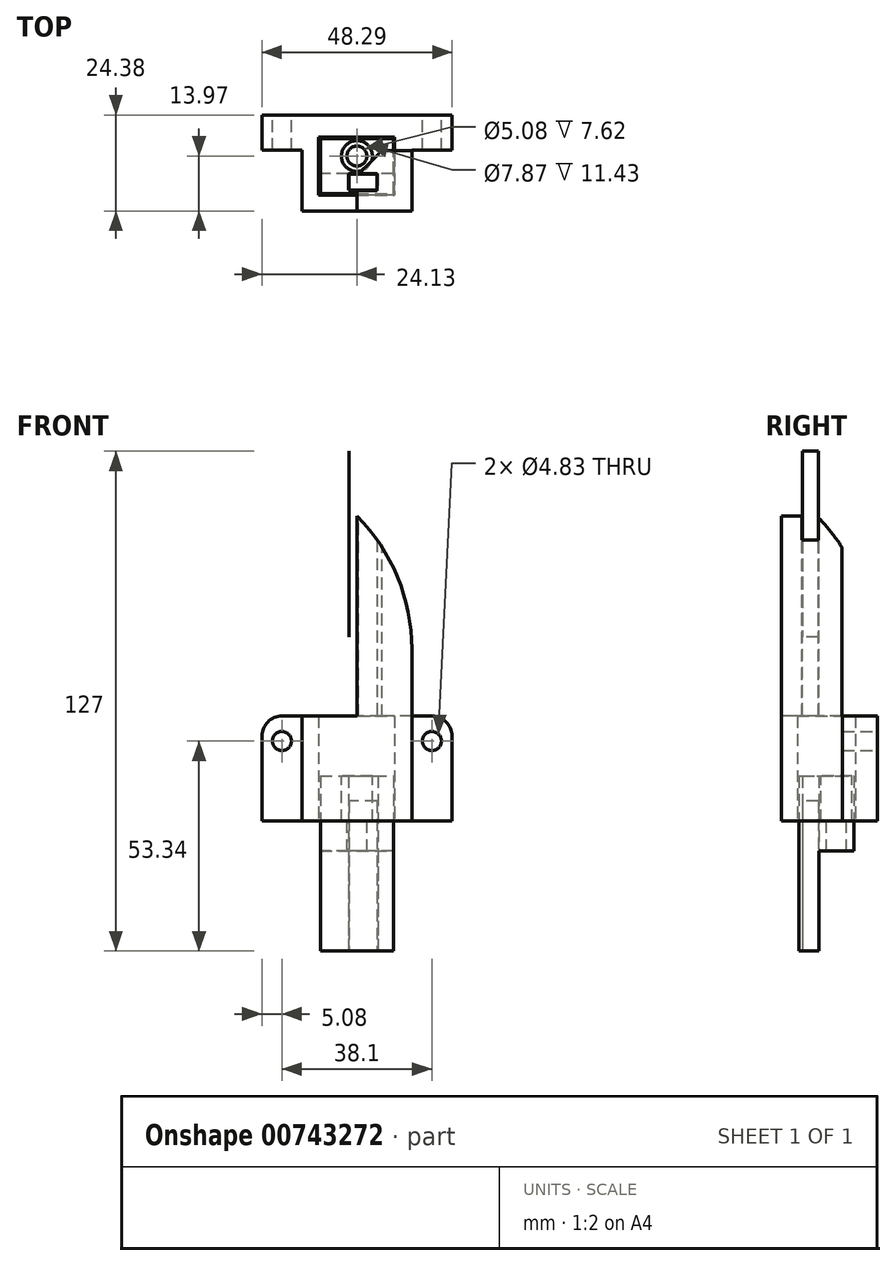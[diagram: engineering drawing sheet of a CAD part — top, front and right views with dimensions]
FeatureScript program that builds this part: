
annotation { "Feature Type Name" : "Feature", "Feature Type Description" : "" }
export const myFeature = defineFeature(function(context is Context, id is Id, definition is map)
    precondition{}
    {
        {
            var Q0;
            Q0=qCreatedBy(makeId("Top.planeOp"),FACE);
            var sketch = newSketch(context, id + "F0", { "sketchPlane" : qUnion([Q0])});
            skLineSegment(sketch, "E0.bottom", {"start": v(-9.27, -4.45) * mm, "end": v(9.27, -4.45) * mm});
            skLineSegment(sketch, "E0.top", {"start": v(-9.27, 4.45) * mm, "end": v(9.27, 4.45) * mm});
            skLineSegment(sketch, "E0.left", {"start": v(-9.27, -4.45) * mm, "end": v(-9.27, 4.45) * mm});
            skLineSegment(sketch, "E0.right", {"start": v(9.27, -4.45) * mm, "end": v(9.27, 4.45) * mm});
            skPoint(sketch, "E0.middle", {"position": v(0, 0) * mm});
            skSolve(sketch);
        }
        {
            var Q0;
            Q0 = qSketchRegion(id + "F0", true);
            extrude(context, id + "F1", {"entities" : qUnion([Q0]), "depth" : 6.35 * mm, "offsetDistance" : 25.4 * mm});
        }
        {
            var Q0;
            Q0=makeQuery(id+"F1.opExtrude","SWEPT_FACE",FACE,{"disambiguationData":[OSD([sQuery(id+"F0.wireOp",EDGE,"E0.bottom")])]});
            extrude(context, id + "F2", {"entities" : qUnion([Q0]), "operationType" : NewBodyOperationType.ADD, "depth" : 5.08 * mm, "offsetDistance" : 25.4 * mm});
        }
        {
            var Q0;
            {var subQ0=sQuery(id+"F0.wireOp",EDGE,"E0.bottom");Q0=makeQuery(id+"F2.boolean.opBoolean","MERGE",FACE,{"derivedFrom":[makeQuery(id+"F1.opExtrude","CAP_FACE",FACE,{"disambiguationData":[OSD([subQ0,sQuery(id+"F0.wireOp",EDGE,"E0.top"),sQuery(id+"F0.wireOp",EDGE,"E0.left"),sQuery(id+"F0.wireOp",EDGE,"E0.right")])],"isStart":true}),makeQuery(id+"F2.opExtrude","SWEPT_FACE",FACE,{"disambiguationData":[OSD([subQ0]),TDD([makeQuery(id+"F1.opExtrude","CAP_EDGE",EDGE,{"disambiguationData":[OSD([subQ0])],"isStart":true})])]})]});}
            var sketch = newSketch(context, id + "F3", { "sketchPlane" : qUnion([Q0])});
            skLineSegment(sketch, "E1.bottom", {"start": v(9.27, 9.53) * mm, "end": v(-9.27, 9.53) * mm});
            skLineSegment(sketch, "E1.top", {"start": v(9.27, 4.46) * mm, "end": v(-9.27, 4.46) * mm});
            skLineSegment(sketch, "E1.left", {"start": v(9.27, 9.53) * mm, "end": v(9.27, 4.46) * mm});
            skLineSegment(sketch, "E1.right", {"start": v(-9.27, 9.53) * mm, "end": v(-9.27, 4.46) * mm});
            skSolve(sketch);
        }
        {
            var Q0;
            Q0 = qSketchRegion(id + "F3", true);
            extrude(context, id + "F4", {"entities" : qUnion([Q0]), "operationType" : NewBodyOperationType.ADD, "depth" : 25.4 * mm, "offsetDistance" : 25.4 * mm});
        }
        {
            var Q0;
            Q0=makeQuery(id+"F4.opExtrude","CAP_FACE",FACE,{"disambiguationData":[OSD([sQuery(id+"F3.wireOp",EDGE,"E1.bottom"),sQuery(id+"F3.wireOp",EDGE,"E1.top"),sQuery(id+"F3.wireOp",EDGE,"E1.left"),sQuery(id+"F3.wireOp",EDGE,"E1.right")])],"isStart":false});
            var sketch = newSketch(context, id + "F5", { "sketchPlane" : qUnion([Q0])});
            skLineSegment(sketch, "E2.bottom", {"start": v(-2.13, 4.46) * mm, "end": v(5.36, 4.46) * mm});
            skLineSegment(sketch, "E2.top", {"start": v(-2.13, 8.65) * mm, "end": v(5.36, 8.65) * mm});
            skLineSegment(sketch, "E2.left", {"start": v(-2.13, 4.46) * mm, "end": v(-2.13, 8.65) * mm});
            skLineSegment(sketch, "E2.right", {"start": v(5.36, 4.46) * mm, "end": v(5.36, 8.65) * mm});
            skSolve(sketch);
        }
        {
            var Q0;
            Q0 = qSketchRegion(id + "F5", true);
            extrude(context, id + "F6", {"entities" : qUnion([Q0]), "operationType" : NewBodyOperationType.REMOVE, "oppositeDirection" : true, "depth" : 125.22 * mm, "offsetDistance" : 25.4 * mm});
        }
        {
            var Q0;
            {var subQ0=sQuery(id+"F0.wireOp",EDGE,"E0.bottom");Q0=makeQuery(id+"F2.boolean.opBoolean","MERGE",FACE,{"derivedFrom":[makeQuery(id+"F1.opExtrude","CAP_FACE",FACE,{"disambiguationData":[OSD([subQ0,sQuery(id+"F0.wireOp",EDGE,"E0.top"),sQuery(id+"F0.wireOp",EDGE,"E0.left"),sQuery(id+"F0.wireOp",EDGE,"E0.right")])],"isStart":false}),makeQuery(id+"F2.opExtrude","SWEPT_FACE",FACE,{"disambiguationData":[OSD([subQ0]),TDD([makeQuery(id+"F1.opExtrude","CAP_EDGE",EDGE,{"disambiguationData":[OSD([subQ0])],"isStart":false})])]})]});}
            extrude(context, id + "F7", {"entities" : qUnion([Q0]), "operationType" : NewBodyOperationType.ADD, "depth" : 6.35 * mm, "offsetDistance" : 25.4 * mm});
        }
        {
            var Q0;
            Q0=makeQuery(id+"F4.opExtrude","CAP_FACE",FACE,{"disambiguationData":[OSD([sQuery(id+"F3.wireOp",EDGE,"E1.bottom"),sQuery(id+"F3.wireOp",EDGE,"E1.top"),sQuery(id+"F3.wireOp",EDGE,"E1.left"),sQuery(id+"F3.wireOp",EDGE,"E1.right")])],"isStart":false});
            var sketch = newSketch(context, id + "F8", { "sketchPlane" : qUnion([Q0])});
            skLineSegment(sketch, "E3.bottom", {"start": v(-1.98, 8.65) * mm, "end": v(5.06, 8.65) * mm});
            skLineSegment(sketch, "E3.top", {"start": v(-1.98, 4.6) * mm, "end": v(5.06, 4.6) * mm});
            skLineSegment(sketch, "E3.left", {"start": v(-1.98, 8.65) * mm, "end": v(-1.98, 4.6) * mm});
            skLineSegment(sketch, "E3.right", {"start": v(5.06, 8.65) * mm, "end": v(5.06, 4.6) * mm});
            skSolve(sketch);
        }
        {
            var Q0;
            Q0 = qSketchRegion(id + "F8", true);
            extrude(context, id + "F9", {"entities" : qUnion([Q0]), "oppositeDirection" : true, "depth" : 127 * mm, "offsetDistance" : 25.4 * mm});
        }
        {
            var Q0;
            Q0=makeQuery(id+"F7.opExtrude","CAP_FACE",FACE,{"disambiguationData":[OSD([sQuery(id+"F0.wireOp",EDGE,"E0.bottom"),sQuery(id+"F0.wireOp",EDGE,"E0.top"),sQuery(id+"F0.wireOp",EDGE,"E0.left"),sQuery(id+"F0.wireOp",EDGE,"E0.right")])],"isStart":false});
            var sketch = newSketch(context, id + "F10", { "sketchPlane" : qUnion([Q0])});
            skLineSegment(sketch, "E4", {"start": v(-24.13, 0) * mm, "end": v(-24.13, 5.97) * mm});
            skLineSegment(sketch, "E5.bottom", {"start": v(-24.13, 5.97) * mm, "end": v(24.16, 5.97) * mm});
            skLineSegment(sketch, "E5.top", {"start": v(-24.13, -13.97) * mm, "end": v(24.16, -13.97) * mm});
            skLineSegment(sketch, "E5.left", {"start": v(-24.13, 5.97) * mm, "end": v(-24.13, -13.97) * mm});
            skLineSegment(sketch, "E5.right", {"start": v(24.16, 5.97) * mm, "end": v(24.16, -13.97) * mm});
            skSolve(sketch);
        }
        {
            var Q0;
            Q0 = qSketchRegion(id + "F10", true);
            extrude(context, id + "F11", {"entities" : qUnion([Q0]), "depth" : 21.59 * mm, "offsetDistance" : 25.4 * mm});
        }
        {
            var Q0;
            Q0=makeQuery(id+"F11.opExtrude","SWEPT_FACE",FACE,{"disambiguationData":[OSD([sQuery(id+"F10.wireOp",EDGE,"E5.bottom")])]});
            var sketch = newSketch(context, id + "F12", { "sketchPlane" : qUnion([Q0])});
            skCircle(sketch, "E6", {"center": v(19.05, 27.94) * mm, "radius": 2.41 * mm});
            skCircle(sketch, "E7", {"center": v(-19.05, 27.94) * mm, "radius": 2.41 * mm});
            skSolve(sketch);
        }
        {
            var Q0;
            Q0 = qSketchRegion(id + "F12", true);
            extrude(context, id + "F13", {"entities" : qUnion([Q0]), "operationType" : NewBodyOperationType.REMOVE, "oppositeDirection" : true, "depth" : 25.4 * mm, "offsetDistance" : 25.4 * mm});
        }
        {
            var Q0;
            Q0=makeQuery(id+"F11.opExtrude","CAP_FACE",FACE,{"disambiguationData":[OSD([sQuery(id+"F10.wireOp",EDGE,"E5.bottom"),sQuery(id+"F10.wireOp",EDGE,"E5.top"),sQuery(id+"F10.wireOp",EDGE,"E5.left"),sQuery(id+"F10.wireOp",EDGE,"E5.right")])],"isStart":true});
            var sketch = newSketch(context, id + "F14", { "sketchPlane" : qUnion([Q0])});
            skLineSegment(sketch, "E8.bottom", {"start": v(9.6, -4.85) * mm, "end": v(-9.71, -4.85) * mm});
            skLineSegment(sketch, "E8.top", {"start": v(9.6, 9.94) * mm, "end": v(-9.71, 9.94) * mm});
            skLineSegment(sketch, "E8.left", {"start": v(9.6, -4.85) * mm, "end": v(9.6, 9.94) * mm});
            skLineSegment(sketch, "E8.right", {"start": v(-9.71, -4.85) * mm, "end": v(-9.71, 9.94) * mm});
            skSolve(sketch);
        }
        {
            var Q0;
            Q0 = qSketchRegion(id + "F14", true);
            extrude(context, id + "F15", {"entities" : qUnion([Q0]), "operationType" : NewBodyOperationType.REMOVE, "oppositeDirection" : true, "depth" : 41.66 * mm, "offsetDistance" : 25.4 * mm});
        }
        {
            var Q0;
            Q0=makeQuery(id+"F11.opExtrude","SWEPT_FACE",FACE,{"disambiguationData":[OSD([sQuery(id+"F10.wireOp",EDGE,"E5.top")])]});
            var sketch = newSketch(context, id + "F16", { "sketchPlane" : qUnion([Q0])});
            skLineSegment(sketch, "E9.bottom", {"start": v(-24.13, 34.3) * mm, "end": v(-13.95, 34.3) * mm});
            skLineSegment(sketch, "E9.top", {"start": v(-24.13, 12.7) * mm, "end": v(-13.95, 12.7) * mm});
            skLineSegment(sketch, "E9.left", {"start": v(-24.13, 34.3) * mm, "end": v(-24.13, 12.7) * mm});
            skLineSegment(sketch, "E9.right", {"start": v(-13.95, 34.3) * mm, "end": v(-13.95, 12.7) * mm});
            skLineSegment(sketch, "E10.bottom", {"start": v(24.16, 34.3) * mm, "end": v(13.94, 34.3) * mm});
            skLineSegment(sketch, "E10.top", {"start": v(24.16, 12.7) * mm, "end": v(13.94, 12.7) * mm});
            skLineSegment(sketch, "E10.left", {"start": v(24.16, 34.3) * mm, "end": v(24.16, 12.7) * mm});
            skLineSegment(sketch, "E10.right", {"start": v(13.94, 34.3) * mm, "end": v(13.94, 12.7) * mm});
            skSolve(sketch);
        }
        {
            var Q0;
            Q0 = qSketchRegion(id + "F16", true);
            extrude(context, id + "F17", {"entities" : qUnion([Q0]), "operationType" : NewBodyOperationType.REMOVE, "oppositeDirection" : true, "depth" : 15.5 * mm, "offsetDistance" : 25.4 * mm});
        }
        {
            var Q0;
            Q0=makeQuery(id+"F11.opExtrude","CAP_FACE",FACE,{"disambiguationData":[OSD([sQuery(id+"F10.wireOp",EDGE,"E5.bottom"),sQuery(id+"F10.wireOp",EDGE,"E5.top"),sQuery(id+"F10.wireOp",EDGE,"E5.left"),sQuery(id+"F10.wireOp",EDGE,"E5.right")])],"isStart":true});
            extrude(context, id + "F18", {"entities" : qUnion([Q0]), "operationType" : NewBodyOperationType.ADD, "depth" : 5.08 * mm, "offsetDistance" : 25.4 * mm});
        }
        {
            var Q0;
            Q0=makeQuery(id+"F7.opExtrude","CAP_FACE",FACE,{"disambiguationData":[OSD([sQuery(id+"F0.wireOp",EDGE,"E0.bottom"),sQuery(id+"F0.wireOp",EDGE,"E0.top"),sQuery(id+"F0.wireOp",EDGE,"E0.left"),sQuery(id+"F0.wireOp",EDGE,"E0.right")])],"isStart":false});
            extrude(context, id + "F19", {"entities" : qUnion([Q0]), "operationType" : NewBodyOperationType.ADD, "depth" : 6.35 * mm, "offsetDistance" : 25.4 * mm});
        }
        {
            var Q0;
            Q0=makeQuery(id+"F11.opExtrude","CAP_FACE",FACE,{"disambiguationData":[OSD([sQuery(id+"F10.wireOp",EDGE,"E5.bottom"),sQuery(id+"F10.wireOp",EDGE,"E5.top"),sQuery(id+"F10.wireOp",EDGE,"E5.left"),sQuery(id+"F10.wireOp",EDGE,"E5.right")])],"isStart":false});
            var sketch = newSketch(context, id + "F20", { "sketchPlane" : qUnion([Q0])});
            skLineSegment(sketch, "E11.bottom", {"start": v(13.94, 1.4) * mm, "end": v(0, 1.4) * mm});
            skLineSegment(sketch, "E11.top", {"start": v(13.94, -13.97) * mm, "end": v(0, -13.97) * mm});
            skLineSegment(sketch, "E11.left", {"start": v(13.94, 1.4) * mm, "end": v(13.94, -13.97) * mm});
            skLineSegment(sketch, "E11.right", {"start": v(0, 1.4) * mm, "end": v(0, -13.97) * mm});
            skSolve(sketch);
        }
        {
            var Q0;
            Q0 = qSketchRegion(id + "F20", true);
            extrude(context, id + "F21", {"entities" : qUnion([Q0]), "operationType" : NewBodyOperationType.ADD, "depth" : 50.8 * mm, "offsetDistance" : 25.4 * mm});
        }
        {
            var Q0;
            Q0=makeQuery(id+"F21.opExtrude","CAP_EDGE",EDGE,{"disambiguationData":[OSD([sQuery(id+"F20.wireOp",EDGE,"E11.left")])],"isStart":false});
            fillet(context, id + "F22", {"entities" : qUnion([Q0]), "radius" : 47.83 * mm, "tangentPropagation" : true, "allowEdgeOverflow" : false});
        }
        {
            var Q0;
            Q0=makeQuery(id+"F21.opExtrude","SWEPT_EDGE",EDGE,{"disambiguationData":[OSD([sQuery(id+"F20.wireOp",EDGE,"E11.bottom"),sQuery(id+"F20.wireOp",EDGE,"E11.right")])]});
            chamfer(context, id + "F23", {"entities" : qUnion([Q0]), "width" : 6.35 * mm, "tangentPropagation" : true});
        }
        {
            var Q0;
            Q0=makeQuery(id+"F11.opExtrude","CAP_EDGE",EDGE,{"disambiguationData":[OSD([sQuery(id+"F10.wireOp",EDGE,"E5.left")])],"isStart":false});
            var Q1;
            Q1=makeQuery(id+"F11.opExtrude","CAP_EDGE",EDGE,{"disambiguationData":[OSD([sQuery(id+"F10.wireOp",EDGE,"E5.right")])],"isStart":false});
            fillet(context, id + "F24", {"entities" : qUnion([Q0, Q1]), "radius" : 5.08 * mm, "tangentPropagation" : true, "allowEdgeOverflow" : false});
        }
        {
            var Q0;
            Q0=makeQuery(id+"F11.opExtrude","CAP_FACE",FACE,{"disambiguationData":[OSD([sQuery(id+"F10.wireOp",EDGE,"E5.bottom"),sQuery(id+"F10.wireOp",EDGE,"E5.top"),sQuery(id+"F10.wireOp",EDGE,"E5.left"),sQuery(id+"F10.wireOp",EDGE,"E5.right")])],"isStart":false});
            var sketch = newSketch(context, id + "F25", { "sketchPlane" : qUnion([Q0])});
            skLineSegment(sketch, "E12.bottom", {"start": v(-1.97, -4.51) * mm, "end": v(5.15, -4.51) * mm});
            skLineSegment(sketch, "E12.top", {"start": v(-1.97, -8.77) * mm, "end": v(5.15, -8.77) * mm});
            skLineSegment(sketch, "E12.left", {"start": v(-1.97, -4.51) * mm, "end": v(-1.97, -8.77) * mm});
            skLineSegment(sketch, "E12.right", {"start": v(5.15, -4.51) * mm, "end": v(5.15, -8.77) * mm});
            skSolve(sketch);
        }
        {
            var Q0;
            Q0 = qSketchRegion(id + "F25", true);
            extrude(context, id + "F26", {"entities" : qUnion([Q0]), "operationType" : NewBodyOperationType.REMOVE, "depth" : 73.15 * mm, "offsetDistance" : 25.4 * mm});
        }
        {
            var Q0;
            {var subQ0=sQuery(id+"F10.wireOp",EDGE,"E5.bottom");Q0=makeQuery(id+"F18.boolean.opBoolean","MERGE",FACE,{"derivedFrom":[makeQuery(id+"F11.opExtrude","SWEPT_FACE",FACE,{"disambiguationData":[OSD([subQ0])]}),makeQuery(id+"F18.opExtrude","SWEPT_FACE",FACE,{"disambiguationData":[OSD([subQ0])]})]});}
            extrude(context, id + "F27", {"entities" : qUnion([Q0]), "operationType" : NewBodyOperationType.ADD, "depth" : 4.44 * mm, "offsetDistance" : 25.4 * mm});
        }
        {
            var Q0;
            Q0=makeQuery(id+"F19.opExtrude","CAP_FACE",FACE,{"disambiguationData":[OSD([sQuery(id+"F0.wireOp",EDGE,"E0.bottom"),sQuery(id+"F0.wireOp",EDGE,"E0.top"),sQuery(id+"F0.wireOp",EDGE,"E0.left"),sQuery(id+"F0.wireOp",EDGE,"E0.right")])],"isStart":false});
            var sketch = newSketch(context, id + "F28", { "sketchPlane" : qUnion([Q0])});
            skCircle(sketch, "E13", {"center": v(0, 0) * mm, "radius": 2.54 * mm});
            skSolve(sketch);
        }
        {
            var Q0;
            Q0=makeQuery(id+"F28.imprint","IMPRINT",FACE,{"disambiguationData":[TD([[makeQuery(id+"F28.imprint","IMPRINT",EDGE,{"derivedFrom":sQuery(id+"F28.wireOp",EDGE,"E13")}),-1.0]])]});
            var sketch = newSketch(context, id + "F29", { "sketchPlane" : qUnion([Q0])});
            skCircle(sketch, "E14", {"center": v(0, 0) * mm, "radius": 3.94 * mm});
            skSolve(sketch);
        }
        {
            var Q0;
            Q0 = qSketchRegion(id + "F28", true);
            extrude(context, id + "F30", {"entities" : qUnion([Q0]), "operationType" : NewBodyOperationType.REMOVE, "oppositeDirection" : true, "depth" : 25.4 * mm, "offsetDistance" : 25.4 * mm});
        }
        {
            var Q0;
            Q0 = qSketchRegion(id + "F29", true);
            extrude(context, id + "F31", {"entities" : qUnion([Q0]), "operationType" : NewBodyOperationType.REMOVE, "oppositeDirection" : true, "depth" : 11.43 * mm, "offsetDistance" : 25.4 * mm});
        }
    });
